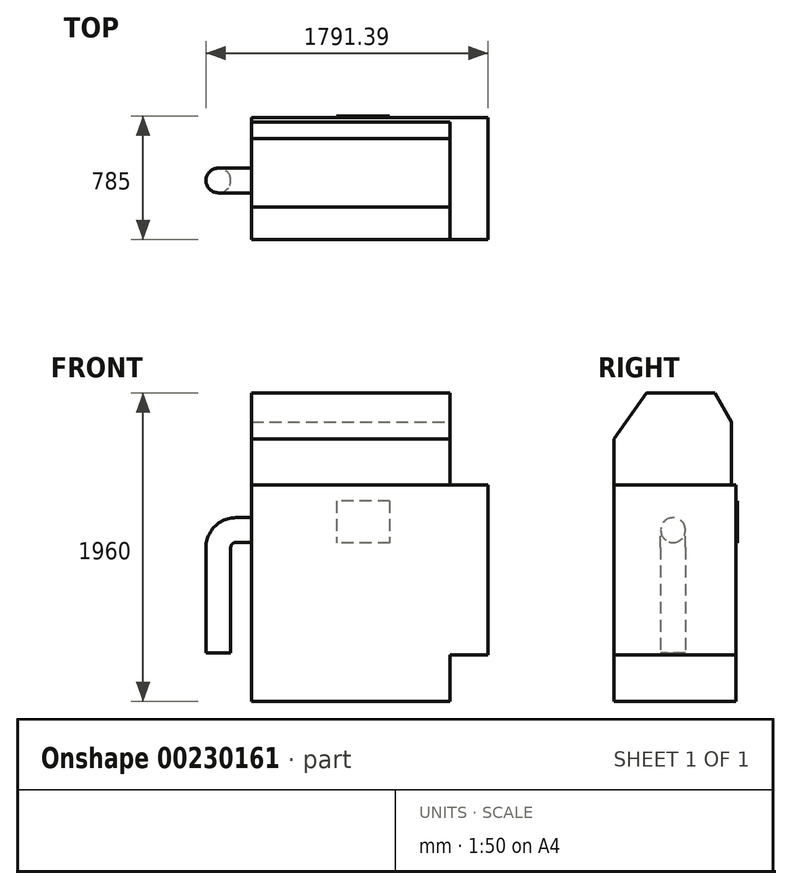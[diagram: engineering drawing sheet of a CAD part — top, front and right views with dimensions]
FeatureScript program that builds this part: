
annotation { "Feature Type Name" : "Feature", "Feature Type Description" : "" }
export const myFeature = defineFeature(function(context is Context, id is Id, definition is map)
    precondition{}
    {
        {
            var Q0;
            Q0=qCreatedBy(makeId("Top.planeOp"),FACE);
            var sketch = newSketch(context, id + "F0", { "sketchPlane" : qUnion([Q0])});
            skLineSegment(sketch, "E0.bottom", {"start": v(751, 375) * mm, "end": v(-751, 375) * mm});
            skLineSegment(sketch, "E0.top", {"start": v(751, -375) * mm, "end": v(-751, -375) * mm});
            skLineSegment(sketch, "E0.left", {"start": v(751, 375) * mm, "end": v(751, -375) * mm});
            skLineSegment(sketch, "E0.right", {"start": v(-751, 375) * mm, "end": v(-751, -375) * mm});
            skPoint(sketch, "E0.middle", {"position": v(0, 0) * mm});
            skSolve(sketch);
        }
        {
            var Q0;
            Q0=makeQuery(id+"F0.imprint","IMPRINT",FACE,{"disambiguationData":[TD([[makeQuery(id+"F0.imprint","IMPRINT",EDGE,{"derivedFrom":sQuery(id+"F0.wireOp",EDGE,"E0.bottom")}),1.0]])]});
            extrude(context, id + "F1", {"entities" : qUnion([Q0]), "depth" : 1376 * mm});
        }
        {
            var Q0;
            Q0=qCreatedBy(makeId("Front.planeOp"),FACE);
            var sketch = newSketch(context, id + "F2", { "sketchPlane" : qUnion([Q0])});
            skLineSegment(sketch, "E1", {"start": v(-751, 1078.67) * mm, "end": v(-851, 1078.67) * mm});
            skLineSegment(sketch, "E2", {"start": v(-951, 978.67) * mm, "end": v(-951, 308.38) * mm});
            skPoint(sketch, "E3.visualSharp", {"position": v(-951, 1078.67) * mm});
            skArc(sketch, "E3.filletArc", {"start": v(-851, 1078.67) * mm, "mid": v(-921.71, 1049.38) * mm, "end": v(-951, 978.67) * mm});
            skSolve(sketch);
        }
        {
            var Q0;
            Q0=makeQuery(id+"F1.opExtrude","SWEPT_FACE",FACE,{"disambiguationData":[OSD([sQuery(id+"F0.wireOp",EDGE,"E0.right")])]});
            var sketch = newSketch(context, id + "F3", { "sketchPlane" : qUnion([Q0])});
            skCircle(sketch, "E4", {"center": v(0, 1089.31) * mm, "radius": 78.75 * mm});
            skSolve(sketch);
        }
        {
            var Q0;
            Q0=makeQuery(id+"F3.imprint","IMPRINT",FACE,{"disambiguationData":[TD([[makeQuery(id+"F3.imprint","IMPRINT",EDGE,{"derivedFrom":sQuery(id+"F3.wireOp",EDGE,"E4")}),1.0]])]});
            var Q1;
            Q1=sQuery(id+"F2.wireOp",EDGE,"E1");
            var Q2;
            Q2=sQuery(id+"F2.wireOp",EDGE,"E2");
            var Q3;
            Q3=sQuery(id+"F2.wireOp",EDGE,"E3.filletArc");
            sweep(context, id + "F4", {"operationType" : NewBodyOperationType.ADD, "profiles" : qUnion([Q0]), "path" : qUnion([Q1, Q2, Q3])});
        }
        {
            var Q0;
            Q0=makeQuery(id+"F1.opExtrude","SWEPT_FACE",FACE,{"disambiguationData":[OSD([sQuery(id+"F0.wireOp",EDGE,"E0.left")])]});
            var sketch = newSketch(context, id + "F5", { "sketchPlane" : qUnion([Q0])});
            skLineSegment(sketch, "E5.bottom", {"start": v(-375, 0) * mm, "end": v(375, 0) * mm});
            skLineSegment(sketch, "E5.top", {"start": v(-375, 297.21) * mm, "end": v(375, 297.21) * mm});
            skLineSegment(sketch, "E5.left", {"start": v(-375, 0) * mm, "end": v(-375, 297.21) * mm});
            skLineSegment(sketch, "E5.right", {"start": v(375, 0) * mm, "end": v(375, 297.21) * mm});
            skSolve(sketch);
        }
        {
            var Q0;
            Q0 = qSketchRegion(id + "F5", true);
            extrude(context, id + "F6", {"entities" : qUnion([Q0]), "operationType" : NewBodyOperationType.REMOVE, "oppositeDirection" : true, "depth" : 241 * mm});
        }
        {
            var Q0;
            Q0=makeQuery(id+"F6.boolean.opBoolean","COPY",FACE,{"derivedFrom":makeQuery(id+"F6.opExtrude","CAP_FACE",FACE,{"disambiguationData":[OSD([sQuery(id+"F5.wireOp",EDGE,"E5.bottom"),sQuery(id+"F5.wireOp",EDGE,"E5.top"),sQuery(id+"F5.wireOp",EDGE,"E5.left"),sQuery(id+"F5.wireOp",EDGE,"E5.right")])],"isStart":false})});
            var sketch = newSketch(context, id + "F7", { "sketchPlane" : qUnion([Q0])});
            skLineSegment(sketch, "E6.bottom", {"start": v(-374.27, 1376) * mm, "end": v(372.35, 1376) * mm});
            skLineSegment(sketch, "E6.top", {"start": v(-168.92, 1960) * mm, "end": v(267.16, 1960) * mm});
            skLineSegment(sketch, "E6.left", {"start": v(-374.27, 1376) * mm, "end": v(-374.27, 1668) * mm});
            skLineSegment(sketch, "E6.right", {"start": v(372.35, 1376) * mm, "end": v(372.35, 1775.3) * mm});
            skLineSegment(sketch, "E7", {"start": v(-374.27, 1668) * mm, "end": v(-168.92, 1960) * mm});
            skLineSegment(sketch, "E8", {"start": v(267.16, 1960) * mm, "end": v(372.35, 1775.3) * mm});
            skPoint(sketch, "E9.orphan", {"position": v(-374.27, 1960) * mm});
            skSolve(sketch);
        }
        {
            var Q0;
            Q0 = qSketchRegion(id + "F7", true);
            var Q1;
            Q1=makeQuery(id+"F1.opExtrude","SWEPT_FACE",FACE,{"disambiguationData":[OSD([sQuery(id+"F0.wireOp",EDGE,"E0.right")])]});
            extrude(context, id + "F8", {"entities" : qUnion([Q0]), "operationType" : NewBodyOperationType.ADD, "endBound" : BoundingType.UP_TO_SURFACE, "oppositeDirection" : true, "endBoundEntityFace" : qUnion([Q1]), "depth" : 1147 * mm});
        }
        {
            var Q0;
            Q0=makeQuery(id+"F1.opExtrude","SWEPT_FACE",FACE,{"disambiguationData":[OSD([sQuery(id+"F0.wireOp",EDGE,"E0.bottom")])]});
            extrude(context, id + "F9", {"entities" : qUnion([Q0]), "operationType" : NewBodyOperationType.ADD, "depth" : 25 * mm});
        }
        {
            var Q0;
            Q0=makeQuery(id+"F9.opExtrude","CAP_FACE",FACE,{"disambiguationData":[OSD([sQuery(id+"F0.wireOp",EDGE,"E0.bottom")])],"isStart":false});
            var sketch = newSketch(context, id + "F10", { "sketchPlane" : qUnion([Q0])});
            skLineSegment(sketch, "E10.bottom", {"start": v(-126, 1274.5) * mm, "end": v(210.01, 1274.5) * mm});
            skLineSegment(sketch, "E10.top", {"start": v(-126, 1008.23) * mm, "end": v(210.01, 1008.23) * mm});
            skLineSegment(sketch, "E10.left", {"start": v(-126, 1274.5) * mm, "end": v(-126, 1008.23) * mm});
            skLineSegment(sketch, "E10.right", {"start": v(210.01, 1274.5) * mm, "end": v(210.01, 1008.23) * mm});
            skSolve(sketch);
        }
        {
            var Q0;
            Q0 = qSketchRegion(id + "F10", true);
            extrude(context, id + "F11", {"entities" : qUnion([Q0]), "operationType" : NewBodyOperationType.ADD, "depth" : 10 * mm});
        }
    });
